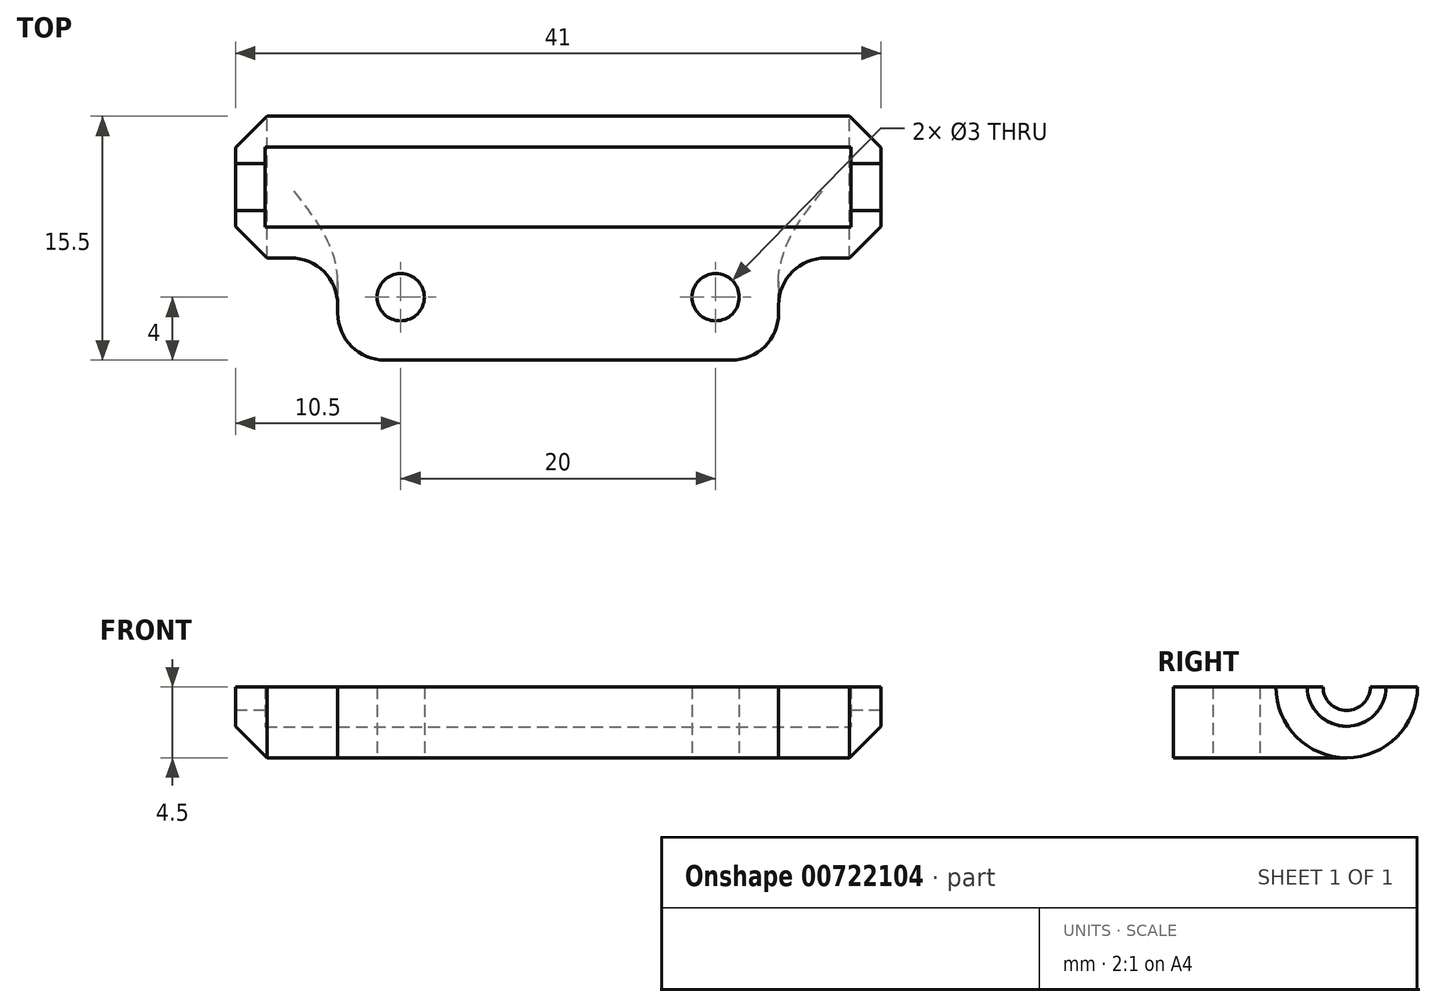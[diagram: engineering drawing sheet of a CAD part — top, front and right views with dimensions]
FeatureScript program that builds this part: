
annotation { "Feature Type Name" : "Feature", "Feature Type Description" : "" }
export const myFeature = defineFeature(function(context is Context, id is Id, definition is map)
    precondition{}
    {
        {
            var Q0;
            Q0=qCreatedBy(makeId("Top.planeOp"),FACE);
            var sketch = newSketch(context, id + "F0", { "sketchPlane" : qUnion([Q0])});
            skCircle(sketch, "E0", {"center": v(10, 0) * mm, "radius": 1.5 * mm});
            skCircle(sketch, "E1.MirrorC", {"center": v(-10, 0) * mm, "radius": 1.5 * mm});
            skLineSegment(sketch, "E2.bottom", {"start": v(14, 11.5) * mm, "end": v(-14, 11.5) * mm});
            skLineSegment(sketch, "E2.top", {"start": v(14, -4) * mm, "end": v(-14, -4) * mm});
            skLineSegment(sketch, "E2.left", {"start": v(14, 2.5) * mm, "end": v(14, -4) * mm});
            skLineSegment(sketch, "E2.right", {"start": v(-14, 2.5) * mm, "end": v(-14, -4) * mm});
            skPoint(sketch, "E2.middle", {"position": v(0, 3.75) * mm});
            skLineSegment(sketch, "E3", {"start": v(-14, 7) * mm, "end": v(14, 7) * mm, "construction": true});
            skLineSegment(sketch, "E4.bottom", {"start": v(20.5, 11.5) * mm, "end": v(14, 11.5) * mm});
            skLineSegment(sketch, "E4.top", {"start": v(20.5, 2.5) * mm, "end": v(-20.5, 2.5) * mm});
            skLineSegment(sketch, "E4.left", {"start": v(20.5, 11.5) * mm, "end": v(20.5, 2.5) * mm});
            skLineSegment(sketch, "E4.right", {"start": v(-20.5, 11.5) * mm, "end": v(-20.5, 2.5) * mm});
            skPoint(sketch, "E4.middle", {"position": v(0, 7) * mm});
            skLineSegment(sketch, "E5.trimOffspring", {"start": v(-14, 11.5) * mm, "end": v(-20.5, 11.5) * mm});
            skSolve(sketch);
        }
        {
            var Q0;
            Q0 = qSketchRegion(id + "F0", true);
            extrude(context, id + "F1", {"entities" : qUnion([Q0]), "depth" : 4.5 * mm, "offsetDistance" : 25 * mm});
        }
        {
            var Q0;
            Q0=qCreatedBy(makeId("Right.planeOp"),FACE);
            var sketch = newSketch(context, id + "F2", { "sketchPlane" : qUnion([Q0])});
            skCircle(sketch, "E6", {"center": v(7, 4.5) * mm, "radius": 2.55 * mm});
            skSolve(sketch);
        }
        {
            var Q0;
            Q0 = qSketchRegion(id + "F2", true);
            extrude(context, id + "F3", {"entities" : qUnion([Q0]), "operationType" : NewBodyOperationType.REMOVE, "oppositeDirection" : true, "depth" : 18.6 * mm, "offsetDistance" : 25 * mm, "hasSecondDirection" : true, "secondDirectionOppositeDirection" : false, "secondDirectionDepth" : 18.6 * mm});
        }
        {
            var Q0;
            Q0=qCreatedBy(makeId("Right.planeOp"),FACE);
            var sketch = newSketch(context, id + "F4", { "sketchPlane" : qUnion([Q0])});
            skCircle(sketch, "E7", {"center": v(7, 4.5) * mm, "radius": 1.5 * mm});
            skLineSegment(sketch, "E8.0", {"start": v(11.5, 4.5) * mm, "end": v(2.5, 4.5) * mm, "construction": true});
            skSolve(sketch);
        }
        {
            var Q0;
            Q0 = qSketchRegion(id + "F4", true);
            extrude(context, id + "F5", {"entities" : qUnion([Q0]), "operationType" : NewBodyOperationType.REMOVE, "endBound" : BoundingType.THROUGH_ALL, "depth" : 25 * mm, "offsetDistance" : 25 * mm, "hasSecondDirection" : true, "secondDirectionBound" : SecondDirectionBoundingType.THROUGH_ALL, "secondDirectionOppositeDirection" : true, "secondDirectionDepth" : 25 * mm});
        }
        {
            var Q0;
            {var subQ0=sQuery(id+"F0.wireOp",EDGE,"E4.top");Q0=makeQuery(id+"F1.opExtrude","CAP_EDGE",EDGE,{"disambiguationData":[OSD([subQ0]),TDD([makeQuery(id+"F0.imprint","IMPRINT",EDGE,{"disambiguationData":[TD([[makeQuery(id+"F0.imprint","INTERSECT",VERTEX,{"derivedFrom":[sQuery(id+"F0.wireOp",EDGE,"E2.left"),subQ0]}),1.0]])],"derivedFrom":subQ0})])],"isStart":true});}
            var Q1;
            {var subQ0=sQuery(id+"F0.wireOp",EDGE,"E4.top");Q1=makeQuery(id+"F1.opExtrude","CAP_EDGE",EDGE,{"disambiguationData":[OSD([subQ0]),TDD([makeQuery(id+"F0.imprint","IMPRINT",EDGE,{"disambiguationData":[TD([[makeQuery(id+"F0.imprint","INTERSECT",VERTEX,{"derivedFrom":[sQuery(id+"F0.wireOp",EDGE,"E2.right"),subQ0]}),-1.0]])],"derivedFrom":subQ0})])],"isStart":true});}
            var Q2;
            Q2=makeQuery(id+"F1.opExtrude","CAP_EDGE",EDGE,{"disambiguationData":[OSD([sQuery(id+"F0.wireOp",EDGE,"E2.bottom"),sQuery(id+"F0.wireOp",EDGE,"E4.bottom"),sQuery(id+"F0.wireOp",EDGE,"E5.trimOffspring")])],"isStart":true});
            fillet(context, id + "F6", {"entities" : qUnion([Q0, Q1, Q2]), "radius" : 4.5 * mm, "tangentPropagation" : true, "allowEdgeOverflow" : false});
        }
        {
            var Q0;
            {var subQ0=sQuery(id+"F0.wireOp",EDGE,"E2.left");var subQ1=sQuery(id+"F0.wireOp",EDGE,"E4.top");Q0=makeQuery(id+"F6.opFillet","BLEND_EDGE",EDGE,{"blendedFrom":[makeQuery(id+"F1.opExtrude","CAP_EDGE",EDGE,{"disambiguationData":[OSD([subQ1]),TDD([makeQuery(id+"F0.imprint","IMPRINT",EDGE,{"disambiguationData":[TD([[makeQuery(id+"F0.imprint","INTERSECT",VERTEX,{"derivedFrom":[subQ0,subQ1]}),1.0]])],"derivedFrom":subQ1})])],"isStart":true}),makeQuery(id+"F1.opExtrude","SWEPT_FACE",FACE,{"disambiguationData":[OSD([subQ0])]})],"blendedInto":[makeQuery(id+"F1.opExtrude","SWEPT_FACE",FACE,{"disambiguationData":[OSD([subQ0])]})]});}
            var Q1;
            Q1=makeQuery(id+"F1.opExtrude","SWEPT_EDGE",EDGE,{"disambiguationData":[OSD([sQuery(id+"F0.wireOp",EDGE,"E2.top"),sQuery(id+"F0.wireOp",EDGE,"E2.left")])]});
            var Q2;
            Q2=makeQuery(id+"F1.opExtrude","SWEPT_EDGE",EDGE,{"disambiguationData":[OSD([sQuery(id+"F0.wireOp",EDGE,"E2.top"),sQuery(id+"F0.wireOp",EDGE,"E2.right")])]});
            var Q3;
            {var subQ0=sQuery(id+"F0.wireOp",EDGE,"E2.right");var subQ1=sQuery(id+"F0.wireOp",EDGE,"E4.top");Q3=makeQuery(id+"F6.opFillet","BLEND_EDGE",EDGE,{"blendedFrom":[makeQuery(id+"F1.opExtrude","CAP_EDGE",EDGE,{"disambiguationData":[OSD([subQ1]),TDD([makeQuery(id+"F0.imprint","IMPRINT",EDGE,{"disambiguationData":[TD([[makeQuery(id+"F0.imprint","INTERSECT",VERTEX,{"derivedFrom":[subQ0,subQ1]}),-1.0]])],"derivedFrom":subQ1})])],"isStart":true}),makeQuery(id+"F1.opExtrude","SWEPT_FACE",FACE,{"disambiguationData":[OSD([subQ0])]})],"blendedInto":[makeQuery(id+"F1.opExtrude","SWEPT_FACE",FACE,{"disambiguationData":[OSD([subQ0])]})]});}
            fillet(context, id + "F7", {"entities" : qUnion([Q0, Q1, Q2, Q3]), "radius" : 3 * mm, "tangentPropagation" : true, "allowEdgeOverflow" : false});
        }
        {
            var Q0;
            Q0=makeQuery(id+"F6.opFillet","BLEND_EDGE",EDGE,{"blendedFrom":[makeQuery(id+"F1.opExtrude","CAP_EDGE",EDGE,{"disambiguationData":[OSD([sQuery(id+"F0.wireOp",EDGE,"E2.bottom"),sQuery(id+"F0.wireOp",EDGE,"E4.bottom"),sQuery(id+"F0.wireOp",EDGE,"E5.trimOffspring")])],"isStart":true}),makeQuery(id+"F1.opExtrude","SWEPT_FACE",FACE,{"disambiguationData":[OSD([sQuery(id+"F0.wireOp",EDGE,"E4.left")])]})],"blendedInto":[makeQuery(id+"F1.opExtrude","SWEPT_FACE",FACE,{"disambiguationData":[OSD([sQuery(id+"F0.wireOp",EDGE,"E4.left")])]})]});
            var Q1;
            Q1=makeQuery(id+"F6.opFillet","BLEND_EDGE",EDGE,{"blendedFrom":[makeQuery(id+"F1.opExtrude","CAP_EDGE",EDGE,{"disambiguationData":[OSD([sQuery(id+"F0.wireOp",EDGE,"E2.bottom"),sQuery(id+"F0.wireOp",EDGE,"E4.bottom"),sQuery(id+"F0.wireOp",EDGE,"E5.trimOffspring")])],"isStart":true}),makeQuery(id+"F1.opExtrude","SWEPT_FACE",FACE,{"disambiguationData":[OSD([sQuery(id+"F0.wireOp",EDGE,"E4.right")])]})],"blendedInto":[makeQuery(id+"F1.opExtrude","SWEPT_FACE",FACE,{"disambiguationData":[OSD([sQuery(id+"F0.wireOp",EDGE,"E4.right")])]})]});
            chamfer(context, id + "F8", {"entities" : qUnion([Q0, Q1]), "width" : 2 * mm, "tangentPropagation" : true});
        }
    });
